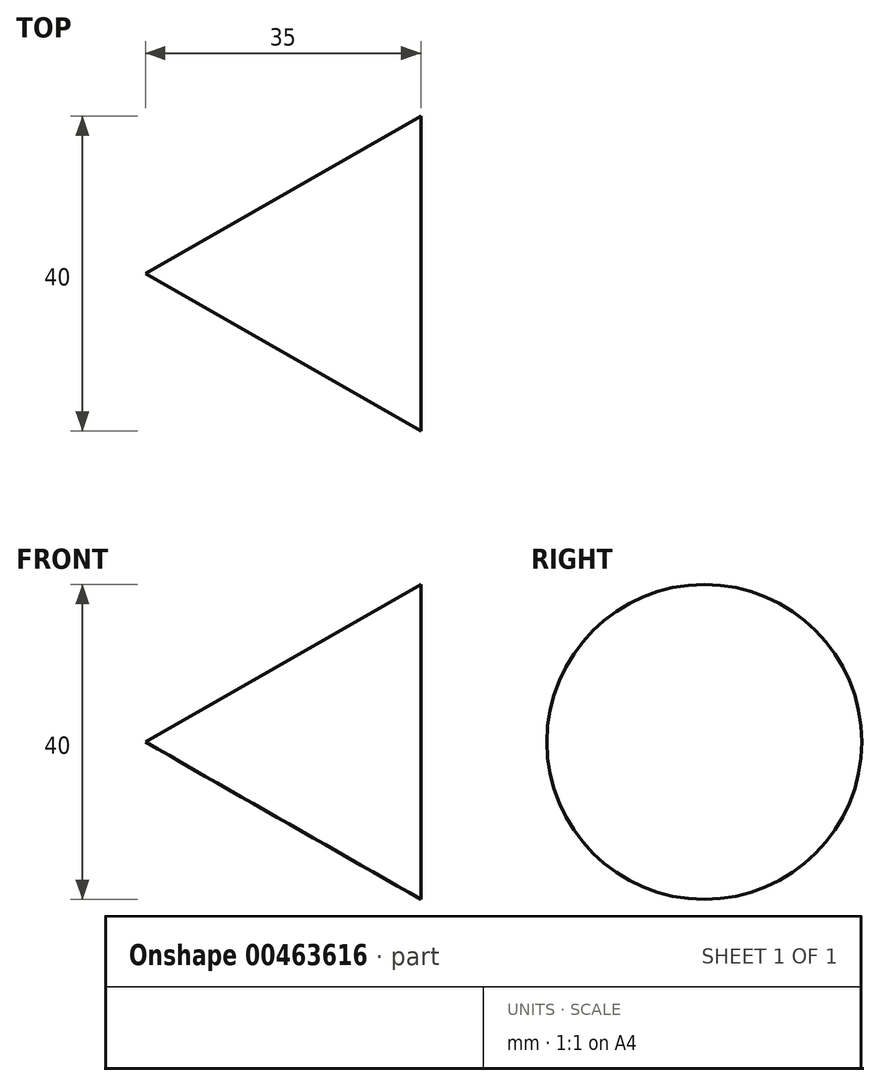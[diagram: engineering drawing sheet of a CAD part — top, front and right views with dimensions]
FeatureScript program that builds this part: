
annotation { "Feature Type Name" : "Feature", "Feature Type Description" : "" }
export const myFeature = defineFeature(function(context is Context, id is Id, definition is map)
    precondition{}
    {
        {
            var Q0;
            Q0=qCreatedBy(makeId("Front.planeOp"),FACE);
            var sketch = newSketch(context, id + "F0", { "sketchPlane" : qUnion([Q0])});
            skLineSegment(sketch, "E0", {"start": v(0, 0) * mm, "end": v(35, 0) * mm});
            skLineSegment(sketch, "E1", {"start": v(35, 0) * mm, "end": v(35, 20) * mm});
            skLineSegment(sketch, "E2", {"start": v(35, 20) * mm, "end": v(0, 0) * mm});
            skSolve(sketch);
        }
        {
            var Q0;
            Q0=makeQuery(id+"F0.imprint","IMPRINT",FACE,{"disambiguationData":[TD([[makeQuery(id+"F0.imprint","IMPRINT",EDGE,{"derivedFrom":sQuery(id+"F0.wireOp",EDGE,"E0")}),1.0]])]});
            var Q1;
            Q1=sQuery(id+"F0.wireOp",EDGE,"E2");
            var Q2;
            Q2=sQuery(id+"F0.wireOp",EDGE,"E0");
            var Q3;
            Q3=sQuery(id+"F0.wireOp",EDGE,"E1");
            var Q4;
            Q4=sQuery(id+"F0.wireOp",EDGE,"E0");
            revolve(context, id + "F1", {"entities" : qUnion([Q0]), "surfaceEntities" : qUnion([Q1, Q2, Q3]), "axis" : qUnion([Q4]), "revolveType" : RevolveType.FULL});
        }
    });
